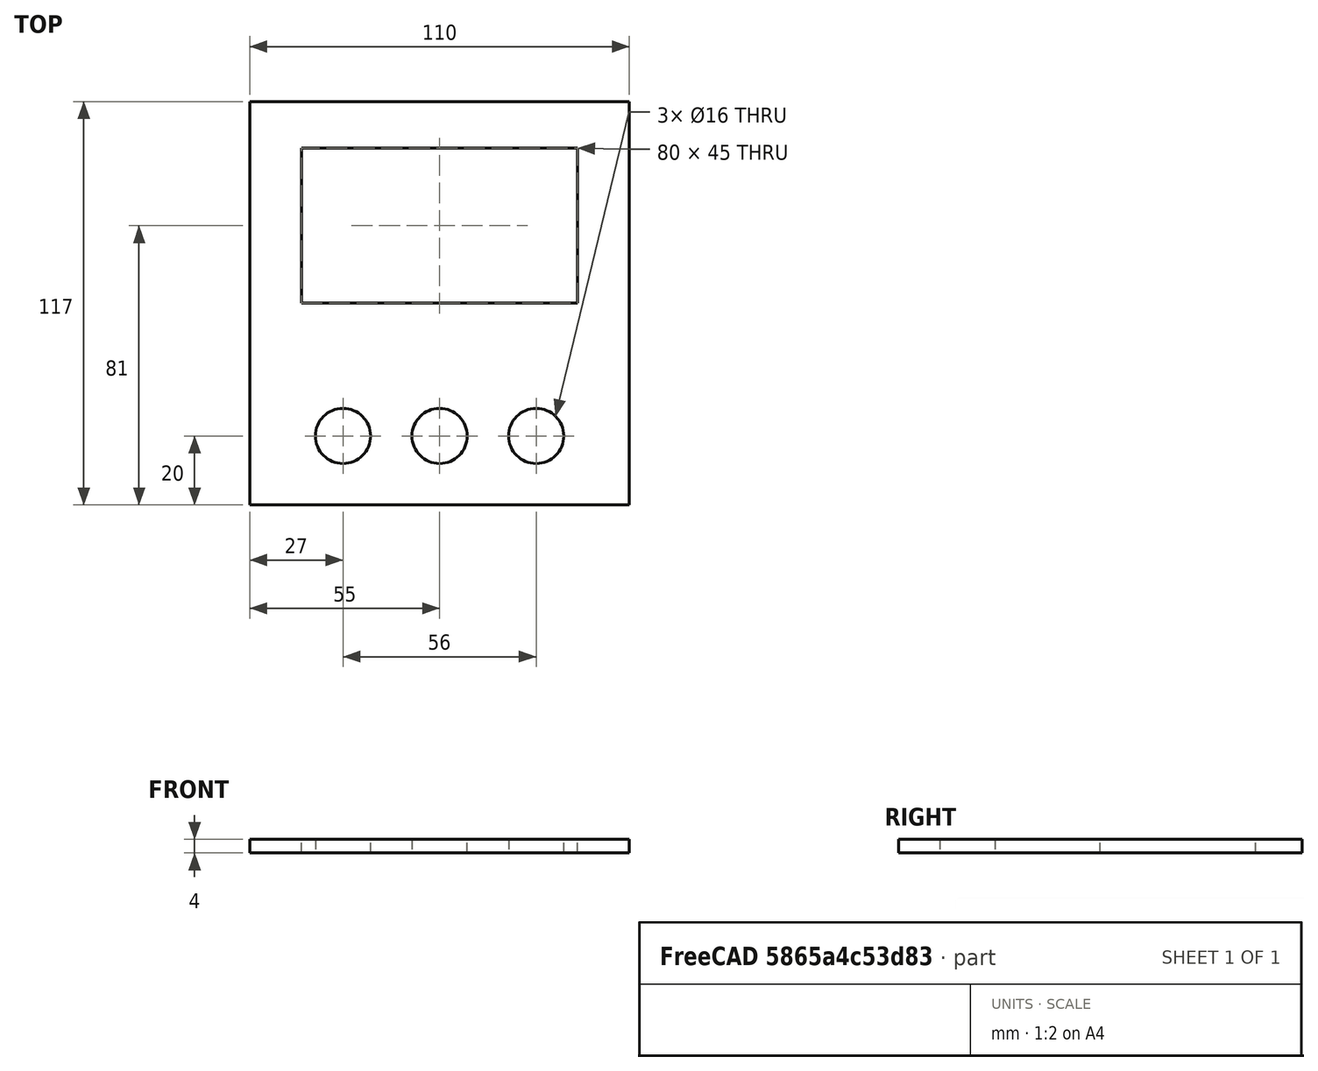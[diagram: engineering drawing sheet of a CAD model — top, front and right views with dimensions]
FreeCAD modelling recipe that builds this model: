
FCSTD DOCUMENT  (FreeCAD 1.0R39319 (Git))
Label: doorbell_cad
License: All rights reserved
LicenseURL: https://en.wikipedia.org/wiki/All_rights_reserved
objects: Spreadsheet::Sheet×1, Sketcher::SketchObject×1, PartDesign::Pad×1, PartDesign::Body×1
note: 6 computed .brp shape members not serialized (recipe doc carries the construction recipe); baked Part::Feature solids carry a one-line shape summary decoded from their .brp

FEATURE [Spreadsheet::Sheet] Spreadsheet  label="Parameters"
  cells = A1(Screen_Width)=80; B1='Screen_Width; A2(Screen_Height)==Screen_Width * 9 / 16; B2='Screen_Height; A3(Padding)=15; B3='Padding; A4(Space_Between)=8; B4='Space_Between; A5(Camera_Diameter)=10; B5='Camera_Diameter; A6(Button_Diameter)=16; B6='Button_Diameter; A7(Panel_Thickness)=4; B7='Panel_Thickness; A8(Button_Spacing)=12; B8='Button_Spacing
FEATURE [Sketcher::SketchObject] Sketch
  ArcFitTolerance = 1e-06
  AttachmentSupport = -> [XY_Plane]
  FullyConstrained = true
  MakeInternals = false
  MapMode = 5
  expr: Constraints[19] = <<Parameters>>.Screen_Width
  expr: Constraints[20] = <<Parameters>>.Screen_Height
  expr: Constraints[23] = <<Parameters>>.Button_Diameter
  expr: Constraints[24] = <<Parameters>>.Screen_Height / 2 + <<Parameters>>.Space_Between + <<Parameters>>.Button_Diameter / 2
  expr: Constraints[25] = <<Parameters>>.Button_Diameter
  expr: Constraints[26] = <<Parameters>>.Screen_Height / 2 + <<Parameters>>.Space_Between + <<Parameters>>.Button_Diameter / 2
  expr: Constraints[27] = <<Parameters>>.Button_Diameter
  expr: Constraints[28] = <<Parameters>>.Screen_Height / 2 + <<Parameters>>.Space_Between + <<Parameters>>.Button_Diameter / 2
  expr: Constraints[29] = <<Parameters>>.Button_Spacing
  expr: Constraints[30] = <<Parameters>>.Button_Spacing
  expr: Constraints[8] = <<Parameters>>.Screen_Width + 2 * <<Parameters>>.Padding
  expr: Constraints[9] = <<Parameters>>.Screen_Height + <<Parameters>>.Camera_Diameter + <<Parameters>>.Button_Diameter + 2 * <<Parameters>>.Space_Between + 2 * <<Parameters>>.Padding
  sketch-geometry (11):
    g0: LineSegment StartX=-55 StartY=58.5 StartZ=0 EndX=-55 EndY=-58.5 EndZ=0
    g1: LineSegment StartX=-55 StartY=-58.5 StartZ=0 EndX=55 EndY=-58.5 EndZ=0
    g2: LineSegment StartX=55 StartY=-58.5 StartZ=0 EndX=55 EndY=58.5 EndZ=0
    g3: LineSegment StartX=55 StartY=58.5 StartZ=0 EndX=-55 EndY=58.5 EndZ=0
    g4: LineSegment StartX=-40 StartY=45 StartZ=0 EndX=-40 EndY=0 EndZ=0
    g5: LineSegment StartX=-40 StartY=0 StartZ=0 EndX=40 EndY=0 EndZ=0
    g6: LineSegment StartX=40 StartY=0 StartZ=0 EndX=40 EndY=45 EndZ=0
    g7: LineSegment StartX=40 StartY=45 StartZ=0 EndX=-40 EndY=45 EndZ=0
    g8: Circle CenterX=0 CenterY=-38.5 CenterZ=0 NormalX=0 NormalY=0 NormalZ=1 AngleXU=0 Radius=8
    g9: Circle CenterX=-28 CenterY=-38.5 CenterZ=0 NormalX=0 NormalY=0 NormalZ=1 AngleXU=0 Radius=8
    g10: Circle CenterX=28 CenterY=-38.5 CenterZ=0 NormalX=0 NormalY=0 NormalZ=1 AngleXU=0 Radius=8
  constraints (31):
    c: Coincident(g0,g1)
    c: Coincident(g1,g2)
    c: Coincident(g2,g3)
    c: Coincident(g3,g0)
    c: Vertical(g0)
    c: Vertical(g2)
    c: Horizontal(g1)
    c: Horizontal(g3)
    c: DistanceX(g3,g3) = 110
    c: DistanceY(g2,g2) = 117
    c: Symmetric(g0,g1,g-1)
    c: Coincident(g4,g5)
    c: Coincident(g5,g6)
    c: Coincident(g6,g7)
    c: Coincident(g7,g4)
    c: Vertical(g4)
    c: Vertical(g6)
    c: Horizontal(g5)
    c: Horizontal(g7)
    c: DistanceX(g7,g7) = 80
    c: DistanceY(g6,g6) = 45
    c: Symmetric(g5,g5,g-1)
    c: PointOnObject(g8,g-2)
    c: Diameter(g8) = 16
    c: Distance(g8,g-1) = 38.5
    c: Diameter(g9) = 16
    c: Distance(g9,g5) = 38.5
    c: Diameter(g10) = 16
    c: Distance(g10,g-1) = 38.5
    c: Distance(g9,g8) = 12
    c: Distance(g8,g10) = 12
FEATURE [PartDesign::Pad] Pad
  Direction = (0,0,1)
  Length = 4
  Length2 = 10
  Profile = -> Sketch
  ReferenceAxis = -> Sketch [N_Axis]
  Refine = true
  Suppressed = false
  Type = 0
  expr: Length = <<Parameters>>.Panel_Thickness
FEATURE [PartDesign::Body] Body
  AllowCompound = false
  Group = -> [Sketch,Pad]
  Origin = -> Origin
  Tip = -> Pad
